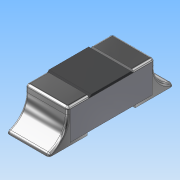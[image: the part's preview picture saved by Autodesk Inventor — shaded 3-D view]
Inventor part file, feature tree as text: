
AUTODESK INVENTOR PART (.ipt)
format: ipt  version: 2016 (Build 200138000, 138)  size: 205,824 bytes
history: native  units: mm
features: extrude x2, fillet x2, sketch x1, mirror x1
ambient origin geometry x8: Origin, YZ Plane, XZ Plane, XY Plane, X Axis, Y Axis, Z Axis, Center Point
bodies: Body1 (feature_tree)
feature tree (6):
  sketch  "Sketch10"  dims[d9=0.499mm d10=0.0mm d11=0.2mm d12=0.45mm d13=0.03mm d14=0.03mm d15=0.25mm d16=45.0deg d17=0.5mm d18=0.0mm d19=0.03mm d21=1.0mm d22=0.4mm d23=0.3mm d24=0.029mm]
  extrude  "Extrusion4"  Depth=0.2mm
  extrude  "Extrusion5"  Depth=0.45mm
  fillet  "Fillet2"  Radius=0.03mm
  fillet  "Fillet3"  Radius=0.03mm
  mirror  "Mirror1"
